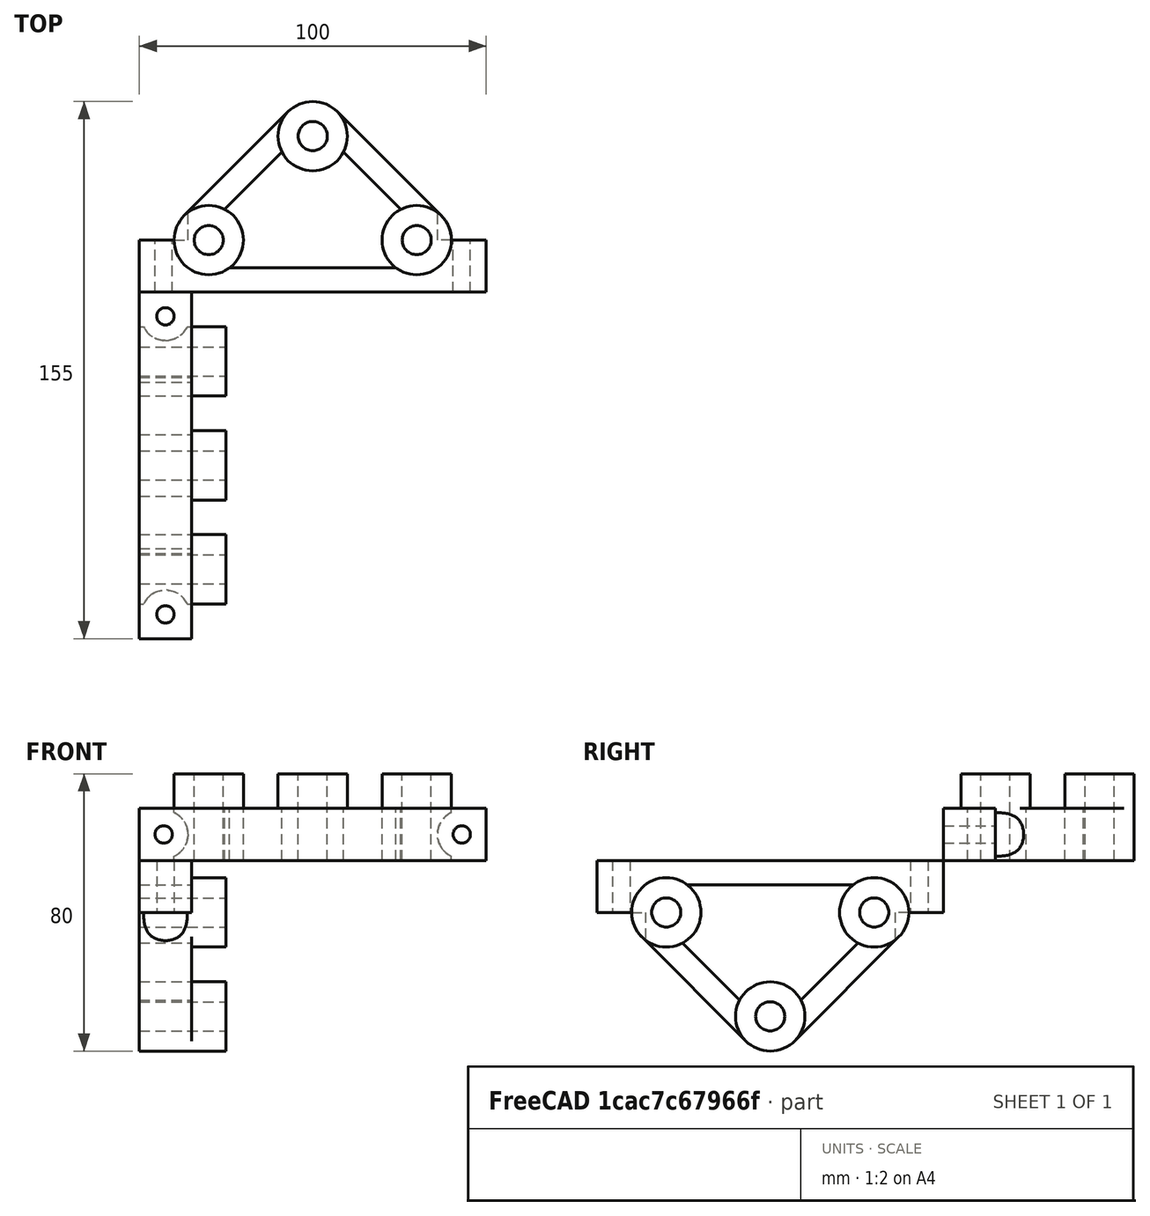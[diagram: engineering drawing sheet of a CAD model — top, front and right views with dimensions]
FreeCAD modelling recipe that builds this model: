
FCSTD DOCUMENT  (FreeCAD 0.15R4527 (Git))
Label: y_frame_inside
License: All rights reserved
LicenseURL: http://es.wikipedia.org/wiki/Todos_los_derechos_reservados
objects: Part::Cylinder×10, Part::MultiFuse×6, Part::Cut×4, Part::Feature×2, Part::Box×2, Mesh::Feature×1, Sketcher::SketchObject×1, Part::Extrusion×1
note: 26 computed .brp shape members not serialized (recipe doc carries the construction recipe); baked Part::Feature solids carry a one-line shape summary decoded from their .brp

FEATURE [Mesh::Feature] frameinside
FEATURE [Part::Feature] frameinside001001  label="frameinside002"
  shape: bbox 100 x 55 x 25 mm, 1742 faces, 0 solids (baked)
FEATURE [Part::Box] Box  label="Cubo"
  Height = 15
  Length = 100
  Width = 15
FEATURE [Part::Cylinder] Cylinder  label="Cilindro"
  Angle = 360
  Height = 25
  Placement = pos=(20,15,0) rot=(0,0,-1;0.785398rad)
  Radius = 10
FEATURE [Part::Cylinder] Cylinder001  label="Cilindro001"
  Angle = 360
  Height = 25
  Placement = pos=(80,15,0) rot=(0,0,-1;0.785398rad)
  Radius = 10
FEATURE [Part::Cylinder] Cylinder002  label="Cilindro002"
  Angle = 360
  Height = 25
  Placement = pos=(50,45,0) rot=(0,0,-1;0.785398rad)
  Radius = 10
FEATURE [Part::MultiFuse] Fusion
  Shapes = -> [Cylinder,Cylinder001,Cylinder002]
FEATURE [Part::Box] Box001  label="Cubo001"
  Height = 15
  Length = 55
  Placement = pos=(24,7,0) rot=(0,0,1;0rad)
  Width = 8
FEATURE [Part::Cut] Cut
  Base = -> Box
  Tool = -> Box001
FEATURE [Part::MultiFuse] Fusion001
  Shapes = -> [Fusion,Cut]
FEATURE [Sketcher::SketchObject] Sketch
  ExternalGeometry = -> [Fusion001]
  Placement = pos=(0,0,0) rot=(1,0,0;3.14159rad)
  Support = -> Fusion001 [Face11]
  sketch-geometry (10):
    g0: LineSegment StartX=12.9289 StartY=-22.0711 StartZ=0 EndX=42.9289 EndY=-52.0711 EndZ=0
    g1: LineSegment StartX=24.624 StartY=-23.8667 StartZ=0 EndX=41.1333 EndY=-40.376 EndZ=0
    g2: LineSegment [constr] StartX=24.624 StartY=-23.8667 StartZ=0 EndX=19.6743 EndY=-28.8164 EndZ=0
    g3: LineSegment StartX=57.0711 StartY=-52.0711 StartZ=0 EndX=87.0711 EndY=-22.0711 EndZ=0
    g4: LineSegment StartX=58.8667 StartY=-40.376 StartZ=0 EndX=75.376 EndY=-23.8667 EndZ=0
    g5: LineSegment [constr] StartX=75.376 StartY=-23.8667 StartZ=0 EndX=80.3257 EndY=-28.8164 EndZ=0
    g6: ArcOfCircle CenterX=50 CenterY=-45 CenterZ=0 NormalX=0 NormalY=0 NormalZ=1 Radius=10 StartAngle=2.66089 EndAngle=3.92699
    g7: ArcOfCircle CenterX=20 CenterY=-15 CenterZ=0 NormalX=0 NormalY=0 NormalZ=1 Radius=10 StartAngle=3.92699 EndAngle=5.19309
    g8: ArcOfCircle CenterX=80 CenterY=-15 CenterZ=0 NormalX=0 NormalY=0 NormalZ=1 Radius=10 StartAngle=4.23168 EndAngle=5.49779
    g9: ArcOfCircle CenterX=50 CenterY=-45 CenterZ=0 NormalX=0 NormalY=0 NormalZ=1 Radius=10 StartAngle=5.49779 EndAngle=6.76389
  constraints (30):
    c: Tangent(g0,g-3) = -1.5708
    c: Tangent(g0,g-4) = -1.5708
    c: PointOnObject(g1,g-4)
    c: PointOnObject(g1,g-3)
    c: Parallel(g1,g0)
    c: Coincident(g2,g1)
    c: PointOnObject(g2,g0)
    c: Perpendicular(g0,g2)
    c: Distance(g2) = 7
    c: Tangent(g3,g-5) = -1.5708
    c: Tangent(g3,g-3) = -1.5708
    c: PointOnObject(g4,g-3)
    c: PointOnObject(g4,g-5)
    c: Parallel(g4,g3)
    c: Coincident(g5,g4)
    c: PointOnObject(g5,g3)
    c: Perpendicular(g3,g5)
    c: Equal(g5,g2)
    c: Coincident(g6,g-3)
    c: Coincident(g6,g1)
    c: Coincident(g6,g0)
    c: Coincident(g7,g-4)
    c: Coincident(g7,g0)
    c: Coincident(g7,g1)
    c: Coincident(g8,g-5)
    c: Coincident(g8,g4)
    c: Coincident(g8,g3)
    c: Coincident(g9,g6)
    c: Coincident(g9,g4)
    c: Coincident(g9,g3)
FEATURE [Part::Cylinder] Cylinder003  label="Cilindro003"
  Angle = 360
  Height = 27
  Placement = pos=(20,15,-1) rot=(0,0,1;0rad)
  Radius = 4.2
FEATURE [Part::Cylinder] Cylinder004  label="Cilindro004"
  Angle = 360
  Height = 27
  Placement = pos=(50,45,-1) rot=(0,0,1;0rad)
  Radius = 4.2
FEATURE [Part::Cylinder] Cylinder005  label="Cilindro005"
  Angle = 360
  Height = 27
  Placement = pos=(80,15,-1) rot=(0,0,1;0rad)
  Radius = 4.2
FEATURE [Part::MultiFuse] Fusion002
  Shapes = -> [Cylinder003,Cylinder005,Cylinder004]
FEATURE [Part::Extrusion] Extrude001
  Base = -> Sketch
  Dir = (0,0,15)
  Solid = true
FEATURE [Part::MultiFuse] Fusion003
  Shapes = -> [Fusion001,Extrude001]
FEATURE [Part::Cut] Cut001
  Base = -> Fusion003
  Tool = -> Fusion002
FEATURE [Part::Cylinder] Cylinder006  label="Cilindro006"
  Angle = 360
  Height = 17
  Placement = pos=(7,-1,7.5) rot=(-1,0,0;1.5708rad)
  Radius = 2.5
FEATURE [Part::Cylinder] Cylinder007  label="Cilindro007"
  Angle = 360
  Height = 17
  Placement = pos=(93,-1,7.5) rot=(-1,0,0;1.5708rad)
  Radius = 2.5
FEATURE [Part::MultiFuse] Fusion004
  Shapes = -> [Cylinder006,Cylinder007]
FEATURE [Part::Cut] Cut002
  Base = -> Cut001
  Tool = -> Fusion004
FEATURE [Part::Cylinder] Cylinder008  label="Cilindro008"
  Angle = 360
  Height = 17
  Placement = pos=(7,15,7.5) rot=(-1,0,0;1.5708rad)
  Radius = 7
FEATURE [Part::Cylinder] Cylinder009  label="Cilindro009"
  Angle = 360
  Height = 17
  Placement = pos=(93,15,7.5) rot=(-1,0,0;1.5708rad)
  Radius = 7
FEATURE [Part::MultiFuse] Fusion005
  Shapes = -> [Cylinder008,Cylinder009]
FEATURE [Part::Cut] Cut003  label="y_frame_inside"
  Base = -> Cut002
  Tool = -> Fusion005
FEATURE [Part::Feature] Cut003001  label="y_frame_inside001"
  Placement = pos=(0,0,0) rot=(-0.57735,0.57735,-0.57735;2.0944rad)
  shape: bbox 25 x 100 x 55 mm, 29 faces (baked)
